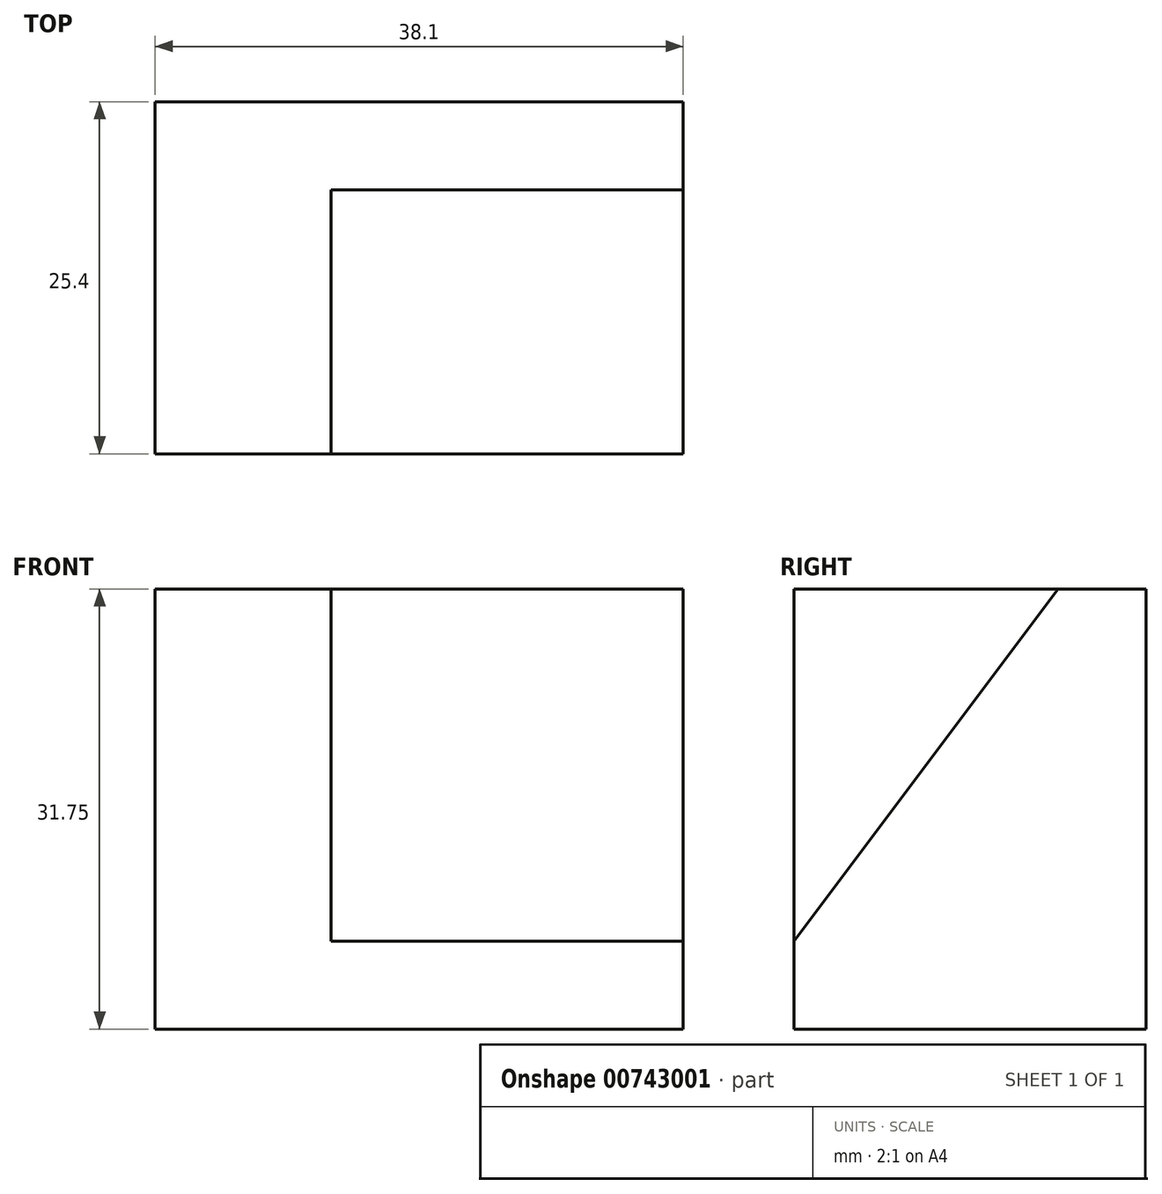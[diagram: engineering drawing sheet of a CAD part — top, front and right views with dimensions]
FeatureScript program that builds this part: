
annotation { "Feature Type Name" : "Feature", "Feature Type Description" : "" }
export const myFeature = defineFeature(function(context is Context, id is Id, definition is map)
    precondition{}
    {
        {
            var Q0;
            Q0=qCreatedBy(makeId("Front.planeOp"),FACE);
            var sketch = newSketch(context, id + "F0", { "sketchPlane" : qUnion([Q0])});
            skLineSegment(sketch, "E0.bottom", {"start": v(0, 0) * mm, "end": v(38.1, 0) * mm});
            skLineSegment(sketch, "E0.top", {"start": v(0, 31.75) * mm, "end": v(38.1, 31.75) * mm});
            skLineSegment(sketch, "E0.left", {"start": v(0, 0) * mm, "end": v(0, 31.75) * mm});
            skLineSegment(sketch, "E0.right", {"start": v(38.1, 0) * mm, "end": v(38.1, 31.75) * mm});
            skSolve(sketch);
        }
        {
            var Q0;
            Q0 = qSketchRegion(id + "F0", true);
            var Q1;
            Q1=makeQuery(id+"F0.imprint","IMPRINT",FACE,{"disambiguationData":[TD([[makeQuery(id+"F0.imprint","IMPRINT",EDGE,{"derivedFrom":sQuery(id+"F0.wireOp",EDGE,"E0.bottom")}),1.0]])]});
            extrude(context, id + "F1", {"entities" : qUnion([Q0, Q1]), "depth" : 25.4 * mm, "offsetDistance" : 25.4 * mm});
        }
        {
            var Q0;
            Q0=makeQuery(id+"F1.opExtrude","SWEPT_FACE",FACE,{"disambiguationData":[OSD([sQuery(id+"F0.wireOp",EDGE,"E0.right")])]});
            var sketch = newSketch(context, id + "F2", { "sketchPlane" : qUnion([Q0])});
            skLineSegment(sketch, "E1.bottom", {"start": v(-25.4, 31.75) * mm, "end": v(-6.35, 31.75) * mm});
            skLineSegment(sketch, "E1.left", {"start": v(-25.4, 31.75) * mm, "end": v(-25.4, 6.35) * mm});
            skLineSegment(sketch, "E2", {"start": v(-25.4, 6.35) * mm, "end": v(-6.35, 31.75) * mm});
            skSolve(sketch);
        }
        {
            var Q0;
            Q0 = qSketchRegion(id + "F2", true);
            extrude(context, id + "F3", {"entities" : qUnion([Q0]), "operationType" : NewBodyOperationType.REMOVE, "oppositeDirection" : true, "depth" : 25.4 * mm, "offsetDistance" : 25.4 * mm});
        }
    });
